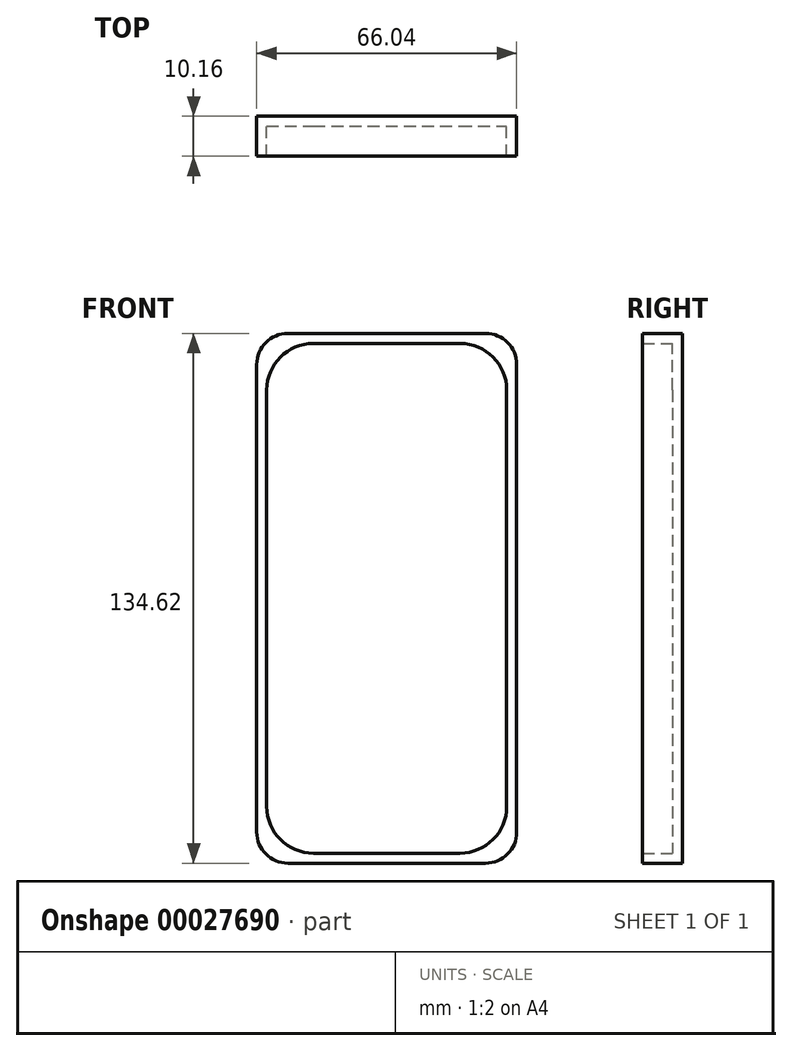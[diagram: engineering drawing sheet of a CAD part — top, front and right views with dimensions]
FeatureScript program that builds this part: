
annotation { "Feature Type Name" : "Feature", "Feature Type Description" : "" }
export const myFeature = defineFeature(function(context is Context, id is Id, definition is map)
    precondition{}
    {
        {
            var Q0;
            Q0=qCreatedBy(makeId("Front.planeOp"),FACE);
            var sketch = newSketch(context, id + "F0", { "sketchPlane" : qUnion([Q0])});
            skLineSegment(sketch, "E0.bottom", {"start": v(-55.64, 55.19) * mm, "end": v(10.4, 55.19) * mm});
            skLineSegment(sketch, "E0.top", {"start": v(-55.64, -79.43) * mm, "end": v(10.4, -79.43) * mm});
            skLineSegment(sketch, "E0.left", {"start": v(-55.64, 55.19) * mm, "end": v(-55.64, -79.43) * mm});
            skLineSegment(sketch, "E0.right", {"start": v(10.4, 55.19) * mm, "end": v(10.4, -79.43) * mm});
            skSolve(sketch);
        }
        {
            var Q0;
            Q0=makeQuery(id+"F0.imprint","IMPRINT",FACE,{"disambiguationData":[TD([[makeQuery(id+"F0.imprint","IMPRINT",EDGE,{"derivedFrom":sQuery(id+"F0.wireOp",EDGE,"E0.bottom")}),-1.0]])]});
            extrude(context, id + "F1", {"entities" : qUnion([Q0]), "depth" : 10.16 * mm});
        }
        {
            var Q0;
            Q0=makeQuery(id+"F1.opExtrude","CAP_FACE",FACE,{"disambiguationData":[OSD([sQuery(id+"F0.wireOp",EDGE,"E0.bottom"),sQuery(id+"F0.wireOp",EDGE,"E0.top"),sQuery(id+"F0.wireOp",EDGE,"E0.left"),sQuery(id+"F0.wireOp",EDGE,"E0.right")])],"isStart":false});
            shell(context, id + "F2", {"entities" : qUnion([Q0]), "thickness" : 2.54 * mm});
        }
        {
            var Q0;
            Q0=makeQuery(id+"F1.opExtrude","SWEPT_EDGE",EDGE,{"disambiguationData":[OSD([sQuery(id+"F0.wireOp",EDGE,"E0.bottom"),sQuery(id+"F0.wireOp",EDGE,"E0.left")])]});
            var Q1;
            Q1=makeQuery(id+"F1.opExtrude","SWEPT_EDGE",EDGE,{"disambiguationData":[OSD([sQuery(id+"F0.wireOp",EDGE,"E0.bottom"),sQuery(id+"F0.wireOp",EDGE,"E0.right")])]});
            var Q2;
            Q2=makeQuery(id+"F1.opExtrude","SWEPT_EDGE",EDGE,{"disambiguationData":[OSD([sQuery(id+"F0.wireOp",EDGE,"E0.top"),sQuery(id+"F0.wireOp",EDGE,"E0.right")])]});
            var Q3;
            Q3=makeQuery(id+"F1.opExtrude","SWEPT_EDGE",EDGE,{"disambiguationData":[OSD([sQuery(id+"F0.wireOp",EDGE,"E0.top"),sQuery(id+"F0.wireOp",EDGE,"E0.left")])]});
            fillet(context, id + "F3", {"entities" : qUnion([Q0, Q1, Q2, Q3]), "radius" : 7.92 * mm, "tangentPropagation" : true, "allowEdgeOverflow" : false});
        }
        {
            var Q0;
            Q0=makeQuery(id+"F2.opShell","OFFSET_EDGE",EDGE,{"disambiguationData":[OSD([sQuery(id+"F0.wireOp",EDGE,"E0.bottom"),sQuery(id+"F0.wireOp",EDGE,"E0.left")])]});
            var Q1;
            Q1=makeQuery(id+"F2.opShell","OFFSET_EDGE",EDGE,{"disambiguationData":[OSD([sQuery(id+"F0.wireOp",EDGE,"E0.bottom"),sQuery(id+"F0.wireOp",EDGE,"E0.right")])]});
            var Q2;
            Q2=makeQuery(id+"F2.opShell","OFFSET_EDGE",EDGE,{"disambiguationData":[OSD([sQuery(id+"F0.wireOp",EDGE,"E0.top"),sQuery(id+"F0.wireOp",EDGE,"E0.right")])]});
            var Q3;
            Q3=makeQuery(id+"F2.opShell","OFFSET_EDGE",EDGE,{"disambiguationData":[OSD([sQuery(id+"F0.wireOp",EDGE,"E0.top"),sQuery(id+"F0.wireOp",EDGE,"E0.left")])]});
            fillet(context, id + "F4", {"entities" : qUnion([Q0, Q1, Q2, Q3]), "radius" : 11.85 * mm, "tangentPropagation" : true, "allowEdgeOverflow" : false});
        }
    });
